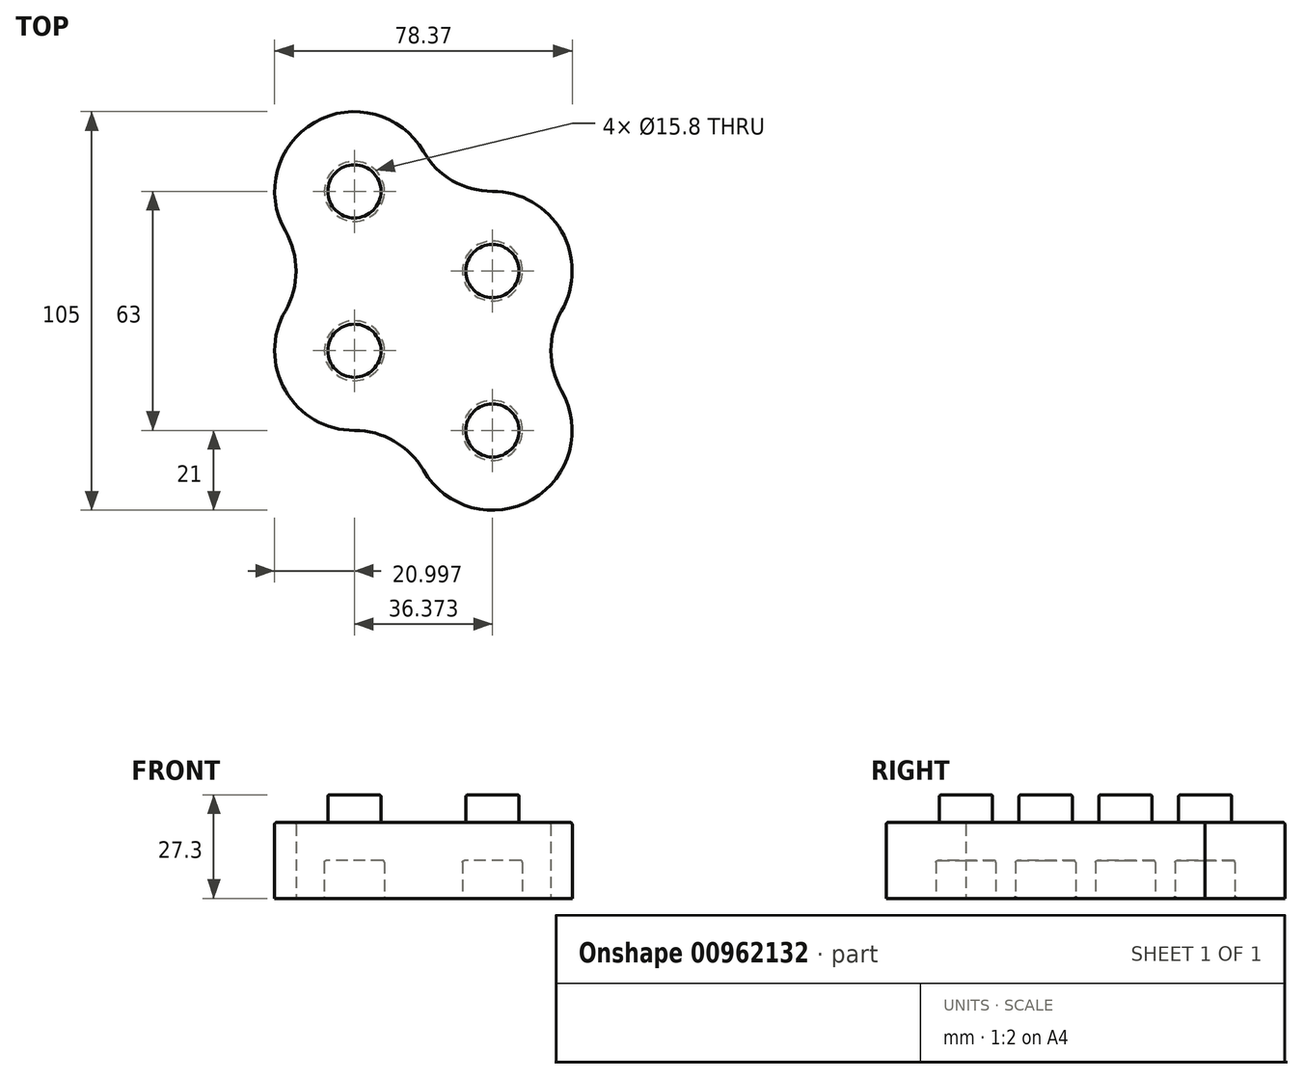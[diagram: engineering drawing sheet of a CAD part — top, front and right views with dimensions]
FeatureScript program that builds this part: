
annotation { "Feature Type Name" : "Feature", "Feature Type Description" : "" }
export const myFeature = defineFeature(function(context is Context, id is Id, definition is map)
    precondition{}
    {
        {
            assignVariable(context, id + "F0", {"name" : "inner_circle_extrude", "anyValue" : 10});
        }
        {
            assignVariable(context, id + "F1", {"name" : "nipple_circle_extrude", "anyValue" : 7.3});
        }
        {
            assignVariable(context, id + "F2", {"name" : "outer_circle_extrude", "anyValue" : 20});
        }
        {
            assignVariable(context, id + "F3", {"name" : "fillet", "anyValue" : 0.5});
        }
        {
            var Q0;
            Q0=qCreatedBy(makeId("Top.planeOp"),FACE);
            var sketch = newSketch(context, id + "F4", { "sketchPlane" : qUnion([Q0])});
            skCircle(sketch, "E0", {"center": v(0, 42) * mm, "radius": 7.9 * mm});
            skCircle(sketch, "E1", {"center": v(0, 0) * mm, "radius": 7.9 * mm});
            skArc(sketch, "E2.converted", {"start": v(18.19, 31.5) * mm, "mid": v(18.19, 52.5) * mm, "end": v(0, 63) * mm});
            skArc(sketch, "E3.converted", {"start": v(-18.19, 10.5) * mm, "mid": v(-18.54, 9.87) * mm, "end": v(-18.87, 9.22) * mm});
            skPoint(sketch, "E4.orphan", {"position": v(-18.87, 9.22) * mm});
            skArc(sketch, "E5.MirrorC", {"start": v(18.19, 10.5) * mm, "mid": v(15.37, 21) * mm, "end": v(18.19, 31.5) * mm});
            skArc(sketch, "E6.converted", {"start": v(-54.56, 31.5) * mm, "mid": v(-54.56, 10.5) * mm, "end": v(-36.37, 0) * mm});
            skArc(sketch, "E7", {"start": v(-18.19, -10.5) * mm, "mid": v(-25.87, -2.81) * mm, "end": v(-36.37, 0) * mm});
            skArc(sketch, "E8.trimOffspring", {"start": v(-18.19, -10.5) * mm, "mid": v(10.5, -18.19) * mm, "end": v(18.19, 10.5) * mm});
            skCircle(sketch, "E9", {"center": v(-36.37, 21) * mm, "radius": 7.9 * mm});
            skArc(sketch, "E10.converted", {"start": v(-18.19, 73.5) * mm, "mid": v(-46.87, 81.19) * mm, "end": v(-54.56, 52.5) * mm});
            skArc(sketch, "E11", {"start": v(-54.56, 31.5) * mm, "mid": v(-51.75, 42) * mm, "end": v(-54.56, 52.5) * mm});
            skArc(sketch, "E12", {"start": v(-18.19, 73.5) * mm, "mid": v(-10.5, 65.81) * mm, "end": v(0, 63) * mm});
            skCircle(sketch, "E13", {"center": v(-36.37, 63) * mm, "radius": 7.9 * mm});
            skSolve(sketch);
        }
        {
            var Q0;
            Q0=makeQuery(id+"F4.imprint","IMPRINT",FACE,{"disambiguationData":[TD([[makeQuery(id+"F4.imprint","IMPRINT",EDGE,{"derivedFrom":sQuery(id+"F4.wireOp",EDGE,"ScaTM9CG-l0WX-AUfX-dH3G-diZ5i2Zft3Bz")}),1.0]])]});
            var Q1;
            Q1=makeQuery(id+"F4.imprint","IMPRINT",FACE,{"disambiguationData":[TD([[makeQuery(id+"F4.imprint","IMPRINT",EDGE,{"derivedFrom":sQuery(id+"F4.wireOp",EDGE,"E0")}),1.0]])]});
            var Q2;
            Q2=makeQuery(id+"F4.imprint","IMPRINT",FACE,{"disambiguationData":[TD([[makeQuery(id+"F4.imprint","IMPRINT",EDGE,{"derivedFrom":sQuery(id+"F4.wireOp",EDGE,"E1")}),1.0]])]});
            var Q3;
            Q3=makeQuery(id+"F4.imprint","IMPRINT",FACE,{"disambiguationData":[TD([[makeQuery(id+"F4.imprint","IMPRINT",EDGE,{"derivedFrom":sQuery(id+"F4.wireOp",EDGE,"E0")}),-1.0]])]});
            var Q4;
            Q4=makeQuery(id+"F4.imprint","IMPRINT",FACE,{"disambiguationData":[TD([[makeQuery(id+"F4.imprint","IMPRINT",EDGE,{"derivedFrom":sQuery(id+"F4.wireOp",EDGE,"E9")}),1.0]])]});
            var Q5;
            Q5=makeQuery(id+"F4.imprint","IMPRINT",FACE,{"disambiguationData":[TD([[makeQuery(id+"F4.imprint","IMPRINT",EDGE,{"derivedFrom":sQuery(id+"F4.wireOp",EDGE,"E13")}),1.0]])]});
            extrude(context, id + "F5", {"entities" : qUnion([Q0, Q1, Q2, Q3, Q4, Q5]), "depth" : (getVariable(context, 'outer_circle_extrude')) * mm, "offsetDistance" : 25 * mm});
        }
        {
            var Q0;
            Q0=makeQuery(id+"F4.imprint","IMPRINT",FACE,{"disambiguationData":[TD([[makeQuery(id+"F4.imprint","IMPRINT",EDGE,{"derivedFrom":sQuery(id+"F4.wireOp",EDGE,"E0")}),1.0]])]});
            var Q1;
            Q1=makeQuery(id+"F4.imprint","IMPRINT",FACE,{"disambiguationData":[TD([[makeQuery(id+"F4.imprint","IMPRINT",EDGE,{"derivedFrom":sQuery(id+"F4.wireOp",EDGE,"E1")}),1.0]])]});
            var Q2;
            Q2=makeQuery(id+"F4.imprint","IMPRINT",FACE,{"disambiguationData":[TD([[makeQuery(id+"F4.imprint","IMPRINT",EDGE,{"derivedFrom":sQuery(id+"F4.wireOp",EDGE,"E9")}),1.0]])]});
            var Q3;
            Q3=makeQuery(id+"F4.imprint","IMPRINT",FACE,{"disambiguationData":[TD([[makeQuery(id+"F4.imprint","IMPRINT",EDGE,{"derivedFrom":sQuery(id+"F4.wireOp",EDGE,"E13")}),1.0]])]});
            extrude(context, id + "F6", {"entities" : qUnion([Q0, Q1, Q2, Q3]), "operationType" : NewBodyOperationType.REMOVE, "depth" : (getVariable(context, 'inner_circle_extrude')) * mm, "offsetDistance" : 25 * mm});
        }
        {
            var Q0;
            Q0=makeQuery(id+"F5.opExtrude","CAP_FACE",FACE,{"disambiguationData":[OSD([sQuery(id+"F4.wireOp",EDGE,"E2.converted"),sQuery(id+"F4.wireOp",EDGE,"E3.converted"),sQuery(id+"F4.wireOp",EDGE,"MIaug4t6-5uLj-SX17-JixO-nkbqJCue0yvX"),sQuery(id+"F4.wireOp",EDGE,"E5.MirrorC")])],"isStart":false});
            var sketch = newSketch(context, id + "F7", { "sketchPlane" : qUnion([Q0])});
            skCircle(sketch, "E14", {"center": v(0, 0) * mm, "radius": 7 * mm});
            skCircle(sketch, "E15", {"center": v(0, 42) * mm, "radius": 7 * mm});
            skCircle(sketch, "E16", {"center": v(-36.37, 21) * mm, "radius": 7 * mm});
            skCircle(sketch, "E17", {"center": v(-36.37, 63) * mm, "radius": 7 * mm});
            skSolve(sketch);
        }
        {
            var Q0;
            Q0=makeQuery(id+"F7.imprint","IMPRINT",FACE,{"disambiguationData":[TD([[makeQuery(id+"F7.imprint","IMPRINT",EDGE,{"derivedFrom":sQuery(id+"F7.wireOp",EDGE,"E14")}),1.0]])]});
            var Q1;
            Q1=makeQuery(id+"F7.imprint","IMPRINT",FACE,{"disambiguationData":[TD([[makeQuery(id+"F7.imprint","IMPRINT",EDGE,{"derivedFrom":sQuery(id+"F7.wireOp",EDGE,"Dg55u7MG-Wcnn-qXMQ-j3jR-78wnB7IFwmOc")}),1.0]])]});
            var Q2;
            Q2=makeQuery(id+"F7.imprint","IMPRINT",FACE,{"disambiguationData":[TD([[makeQuery(id+"F7.imprint","IMPRINT",EDGE,{"derivedFrom":sQuery(id+"F7.wireOp",EDGE,"E15")}),1.0]])]});
            var Q3;
            Q3=makeQuery(id+"F7.imprint","IMPRINT",FACE,{"disambiguationData":[TD([[makeQuery(id+"F7.imprint","IMPRINT",EDGE,{"derivedFrom":sQuery(id+"F7.wireOp",EDGE,"E16")}),1.0]])]});
            var Q4;
            Q4=makeQuery(id+"F7.imprint","IMPRINT",FACE,{"disambiguationData":[TD([[makeQuery(id+"F7.imprint","IMPRINT",EDGE,{"derivedFrom":sQuery(id+"F7.wireOp",EDGE,"E17")}),1.0]])]});
            extrude(context, id + "F8", {"entities" : qUnion([Q0, Q1, Q2, Q3, Q4]), "operationType" : NewBodyOperationType.ADD, "depth" : (getVariable(context, 'nipple_circle_extrude')) * mm, "offsetDistance" : 25 * mm});
        }
        {
            var Q0;
            Q0=makeQuery(id+"F8.opExtrude","CAP_EDGE",EDGE,{"disambiguationData":[OSD([sQuery(id+"F7.wireOp",EDGE,"E14")])],"isStart":false});
            var Q1;
            Q1=makeQuery(id+"F5.opExtrude","CAP_EDGE",EDGE,{"disambiguationData":[OSD([sQuery(id+"F4.wireOp",EDGE,"ScaTM9CG-l0WX-AUfX-dH3G-diZ5i2Zft3Bz")])],"isStart":false});
            var Q2;
            Q2=makeQuery(id+"F5.opExtrude","CAP_EDGE",EDGE,{"disambiguationData":[OSD([sQuery(id+"F4.wireOp",EDGE,"ScaTM9CG-l0WX-AUfX-dH3G-diZ5i2Zft3Bz")])],"isStart":true});
            var Q3;
            Q3=makeQuery(id+"F6.boolean.opBoolean","COPY",EDGE,{"derivedFrom":makeQuery(id+"F6.opExtrude","CAP_EDGE",EDGE,{"disambiguationData":[OSD([sQuery(id+"F4.wireOp",EDGE,"E0")])],"isStart":true})});
            var Q4;
            Q4=makeQuery(id+"F6.boolean.opBoolean","COPY",FACE,{"derivedFrom":makeQuery(id+"F6.opExtrude","CAP_FACE",FACE,{"disambiguationData":[OSD([sQuery(id+"F4.wireOp",EDGE,"E0")])],"isStart":false})});
            var Q5;
            Q5=makeQuery(id+"F6.boolean.opBoolean","COPY",EDGE,{"derivedFrom":makeQuery(id+"F6.opExtrude","CAP_EDGE",EDGE,{"disambiguationData":[OSD([sQuery(id+"F4.wireOp",EDGE,"E1")])],"isStart":true})});
            var Q6;
            Q6=makeQuery(id+"F6.boolean.opBoolean","COPY",EDGE,{"derivedFrom":makeQuery(id+"F6.opExtrude","CAP_EDGE",EDGE,{"disambiguationData":[OSD([sQuery(id+"F4.wireOp",EDGE,"E1")])],"isStart":false})});
            var Q7;
            Q7=makeQuery(id+"F8.opExtrude","CAP_EDGE",EDGE,{"disambiguationData":[OSD([sQuery(id+"F7.wireOp",EDGE,"Dg55u7MG-Wcnn-qXMQ-j3jR-78wnB7IFwmOc")])],"isStart":true});
            var Q8;
            Q8=makeQuery(id+"F8.opExtrude","CAP_EDGE",EDGE,{"disambiguationData":[OSD([sQuery(id+"F7.wireOp",EDGE,"Dg55u7MG-Wcnn-qXMQ-j3jR-78wnB7IFwmOc")])],"isStart":false});
            var Q9;
            Q9=makeQuery(id+"F8.opExtrude","CAP_EDGE",EDGE,{"disambiguationData":[OSD([sQuery(id+"F7.wireOp",EDGE,"E15")])],"isStart":false});
            var Q10;
            Q10=makeQuery(id+"F8.opExtrude","CAP_EDGE",EDGE,{"disambiguationData":[OSD([sQuery(id+"F7.wireOp",EDGE,"E15")])],"isStart":true});
            var Q11;
            Q11=makeQuery(id+"F5.opExtrude","CAP_EDGE",EDGE,{"disambiguationData":[OSD([sQuery(id+"F4.wireOp",EDGE,"E2.converted")])],"isStart":false});
            var Q12;
            Q12=makeQuery(id+"F8.opExtrude","CAP_EDGE",EDGE,{"disambiguationData":[OSD([sQuery(id+"F7.wireOp",EDGE,"E16")])],"isStart":true});
            var Q13;
            Q13=makeQuery(id+"F8.opExtrude","CAP_EDGE",EDGE,{"disambiguationData":[OSD([sQuery(id+"F7.wireOp",EDGE,"E16")])],"isStart":false});
            var Q14;
            Q14=makeQuery(id+"F6.boolean.opBoolean","COPY",FACE,{"derivedFrom":makeQuery(id+"F6.opExtrude","SWEPT_FACE",FACE,{"disambiguationData":[OSD([sQuery(id+"F4.wireOp",EDGE,"E9")])]})});
            var Q15;
            Q15=makeQuery(id+"F8.opExtrude","SWEPT_FACE",FACE,{"disambiguationData":[OSD([sQuery(id+"F7.wireOp",EDGE,"E17")])]});
            var Q16;
            Q16=makeQuery(id+"F6.boolean.opBoolean","COPY",FACE,{"derivedFrom":makeQuery(id+"F6.opExtrude","SWEPT_FACE",FACE,{"disambiguationData":[OSD([sQuery(id+"F4.wireOp",EDGE,"E13")])]})});
            var Q17;
            Q17=makeQuery(id+"F8.opExtrude","SWEPT_FACE",FACE,{"disambiguationData":[OSD([sQuery(id+"F7.wireOp",EDGE,"E14")])]});
            var Q18;
            Q18=makeQuery(id+"F8.opExtrude","CAP_EDGE",EDGE,{"disambiguationData":[OSD([sQuery(id+"F7.wireOp",EDGE,"E14")])],"isStart":true});
            fillet(context, id + "F9", {"entities" : qUnion([Q0, Q1, Q2, Q3, Q4, Q5, Q6, Q7, Q8, Q9, Q10, Q11, Q12, Q13, Q14, Q15, Q16, Q17, Q18]), "radius" : (getVariable(context, 'fillet')) * mm, "tangentPropagation" : true, "allowEdgeOverflow" : false});
        }
    });
